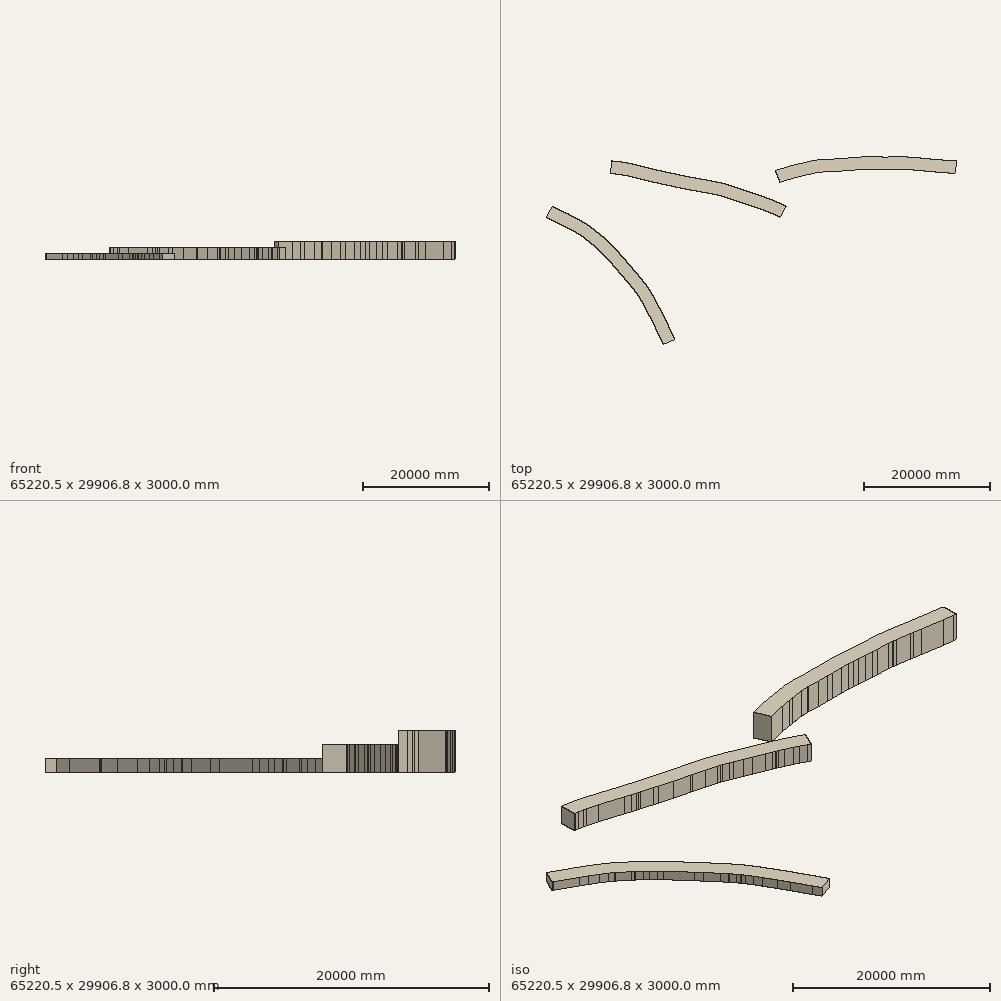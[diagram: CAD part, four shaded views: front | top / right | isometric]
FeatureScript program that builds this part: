
annotation { "Feature Type Name" : "Feature", "Feature Type Description" : "" }
export const myFeature = defineFeature(function(context is Context, id is Id, definition is map)
    precondition{}
    {
        {
            var Q0;
            Q0=qCreatedBy(makeId("Top.planeOp"),FACE);
            var sketch = newSketch(context, id + "F0", { "sketchPlane" : qUnion([Q0])});
            skLineSegment(sketch, "E0", {"start": v(-44615.33, 12253.54) * mm, "end": v(-44554.33, 12247.46) * mm});
            skLineSegment(sketch, "E1", {"start": v(-44554.33, 12247.46) * mm, "end": v(-44050.77, 12191.85) * mm});
            skLineSegment(sketch, "E2", {"start": v(-44050.77, 12191.85) * mm, "end": v(-43383.27, 12133.27) * mm});
            skLineSegment(sketch, "E3", {"start": v(-43383.27, 12133.27) * mm, "end": v(-43116.84, 12094.18) * mm});
            skLineSegment(sketch, "E4", {"start": v(-43116.84, 12094.18) * mm, "end": v(-41654.92, 11815.2) * mm});
            skLineSegment(sketch, "E5", {"start": v(-41654.92, 11815.2) * mm, "end": v(-38646.57, 11078.77) * mm});
            skLineSegment(sketch, "E6", {"start": v(-38646.57, 11078.77) * mm, "end": v(-37801.06, 10858.32) * mm});
            skLineSegment(sketch, "E7", {"start": v(-37801.06, 10858.32) * mm, "end": v(-37268.46, 10749.72) * mm});
            skLineSegment(sketch, "E8", {"start": v(-37268.46, 10749.72) * mm, "end": v(-37019.33, 10693.2) * mm});
            skLineSegment(sketch, "E9", {"start": v(-37019.33, 10693.2) * mm, "end": v(-36702.7, 10624.45) * mm});
            skLineSegment(sketch, "E10", {"start": v(-36702.7, 10624.45) * mm, "end": v(-35235, 10307.82) * mm});
            skLineSegment(sketch, "E11", {"start": v(-35235, 10307.82) * mm, "end": v(-34586.94, 10170.45) * mm});
            skLineSegment(sketch, "E12", {"start": v(-34586.94, 10170.45) * mm, "end": v(-32851.9, 9799.86) * mm});
            skLineSegment(sketch, "E13", {"start": v(-32851.9, 9799.86) * mm, "end": v(-30827.63, 9440.19) * mm});
            skLineSegment(sketch, "E14", {"start": v(-30827.63, 9440.19) * mm, "end": v(-30585.17, 9400.28) * mm});
            skLineSegment(sketch, "E15", {"start": v(-30585.17, 9400.28) * mm, "end": v(-28978.72, 9093.73) * mm});
            skLineSegment(sketch, "E16", {"start": v(-28978.72, 9093.73) * mm, "end": v(-27494.65, 8796.87) * mm});
            skLineSegment(sketch, "E17", {"start": v(-27494.65, 8796.87) * mm, "end": v(-27217.34, 8720.56) * mm});
            skLineSegment(sketch, "E18", {"start": v(-27217.34, 8720.56) * mm, "end": v(-26908.94, 8658.4) * mm});
            skLineSegment(sketch, "E19", {"start": v(-26908.94, 8658.4) * mm, "end": v(-26245.23, 8432.32) * mm});
            skLineSegment(sketch, "E20", {"start": v(-26245.23, 8432.32) * mm, "end": v(-25751.56, 8286.08) * mm});
            skLineSegment(sketch, "E21", {"start": v(-25751.56, 8286.08) * mm, "end": v(-24705.46, 7932.58) * mm});
            skLineSegment(sketch, "E22", {"start": v(-24705.46, 7932.58) * mm, "end": v(-23705.9, 7592.32) * mm});
            skLineSegment(sketch, "E23", {"start": v(-23705.9, 7592.32) * mm, "end": v(-22295.71, 7124.73) * mm});
            skLineSegment(sketch, "E24", {"start": v(-22295.71, 7124.73) * mm, "end": v(-21569.22, 6881.65) * mm});
            skLineSegment(sketch, "E25", {"start": v(-21569.22, 6881.65) * mm, "end": v(-21198.82, 6744) * mm});
            skLineSegment(sketch, "E26", {"start": v(-21198.82, 6744) * mm, "end": v(-21078.3, 6705.9) * mm});
            skLineSegment(sketch, "E27", {"start": v(-21078.3, 6705.9) * mm, "end": v(-20951.53, 6658.56) * mm});
            skLineSegment(sketch, "E28", {"start": v(-20951.53, 6658.56) * mm, "end": v(-20301.1, 6414.34) * mm});
            skLineSegment(sketch, "E29", {"start": v(-20301.1, 6414.34) * mm, "end": v(-19347.36, 6049.93) * mm});
            skLineSegment(sketch, "E30", {"start": v(-19347.36, 6049.93) * mm, "end": v(-18796.29, 5813.54) * mm});
            skLineSegment(sketch, "E31", {"start": v(-18796.29, 5813.54) * mm, "end": v(-18728.97, 5782.95) * mm});
            skLineSegment(sketch, "E32", {"start": v(-18728.97, 5782.95) * mm, "end": v(-17961.13, 5425.9) * mm});
            skLineSegment(sketch, "E33", {"start": v(-17961.13, 5425.9) * mm, "end": v(-17607.02, 5267.78) * mm});
            skLineSegment(sketch, "E34", {"start": v(-44472.78, 14249.25) * mm, "end": v(-44345.25, 14236.52) * mm});
            skLineSegment(sketch, "E35", {"start": v(-44345.25, 14236.52) * mm, "end": v(-43853.56, 14182.23) * mm});
            skLineSegment(sketch, "E36", {"start": v(-43853.56, 14182.23) * mm, "end": v(-43150.5, 14120.53) * mm});
            skLineSegment(sketch, "E37", {"start": v(-43150.5, 14120.53) * mm, "end": v(-42784.07, 14066.77) * mm});
            skLineSegment(sketch, "E38", {"start": v(-42784.07, 14066.77) * mm, "end": v(-41232.01, 13770.58) * mm});
            skLineSegment(sketch, "E39", {"start": v(-41232.01, 13770.58) * mm, "end": v(-41203.7, 13764.5) * mm});
            skLineSegment(sketch, "E40", {"start": v(-41203.7, 13764.5) * mm, "end": v(-41179.88, 13757.96) * mm});
            skLineSegment(sketch, "E41", {"start": v(-41179.88, 13757.96) * mm, "end": v(-38156.48, 13017.85) * mm});
            skLineSegment(sketch, "E42", {"start": v(-38156.48, 13017.85) * mm, "end": v(-37348.64, 12807.23) * mm});
            skLineSegment(sketch, "E43", {"start": v(-37348.64, 12807.23) * mm, "end": v(-36847.33, 12705) * mm});
            skLineSegment(sketch, "E44", {"start": v(-36847.33, 12705) * mm, "end": v(-36585.88, 12645.68) * mm});
            skLineSegment(sketch, "E45", {"start": v(-36585.88, 12645.68) * mm, "end": v(-36279.66, 12579.2) * mm});
            skLineSegment(sketch, "E46", {"start": v(-36279.66, 12579.2) * mm, "end": v(-34816.76, 12263.6) * mm});
            skLineSegment(sketch, "E47", {"start": v(-34816.76, 12263.6) * mm, "end": v(-34170.7, 12126.66) * mm});
            skLineSegment(sketch, "E48", {"start": v(-34170.7, 12126.66) * mm, "end": v(-32467.97, 11762.96) * mm});
            skLineSegment(sketch, "E49", {"start": v(-32467.97, 11762.96) * mm, "end": v(-30490.3, 11411.57) * mm});
            skLineSegment(sketch, "E50", {"start": v(-30490.3, 11411.57) * mm, "end": v(-30235.28, 11369.6) * mm});
            skLineSegment(sketch, "E51", {"start": v(-30235.28, 11369.6) * mm, "end": v(-28595.13, 11056.62) * mm});
            skLineSegment(sketch, "E52", {"start": v(-28595.13, 11056.62) * mm, "end": v(-27032.6, 10744.07) * mm});
            skLineSegment(sketch, "E53", {"start": v(-27032.6, 10744.07) * mm, "end": v(-26753.85, 10667.36) * mm});
            skLineSegment(sketch, "E54", {"start": v(-26753.85, 10667.36) * mm, "end": v(-26386.74, 10593.36) * mm});
            skLineSegment(sketch, "E55", {"start": v(-26386.74, 10593.36) * mm, "end": v(-25638.51, 10338.5) * mm});
            skLineSegment(sketch, "E56", {"start": v(-25638.51, 10338.5) * mm, "end": v(-25147.17, 10192.94) * mm});
            skLineSegment(sketch, "E57", {"start": v(-25147.17, 10192.94) * mm, "end": v(-24063.07, 9826.61) * mm});
            skLineSegment(sketch, "E58", {"start": v(-24063.07, 9826.61) * mm, "end": v(-23068.91, 9488.18) * mm});
            skLineSegment(sketch, "E59", {"start": v(-23068.91, 9488.18) * mm, "end": v(-21663.68, 9022.24) * mm});
            skLineSegment(sketch, "E60", {"start": v(-21663.68, 9022.24) * mm, "end": v(-20903.37, 8767.85) * mm});
            skLineSegment(sketch, "E61", {"start": v(-20903.37, 8767.85) * mm, "end": v(-20548.7, 8636.04) * mm});
            skLineSegment(sketch, "E62", {"start": v(-20548.7, 8636.04) * mm, "end": v(-20426.65, 8597.46) * mm});
            skLineSegment(sketch, "E63", {"start": v(-20426.65, 8597.46) * mm, "end": v(-20250.15, 8531.54) * mm});
            skLineSegment(sketch, "E64", {"start": v(-20250.15, 8531.54) * mm, "end": v(-19592.66, 8284.67) * mm});
            skLineSegment(sketch, "E65", {"start": v(-19592.66, 8284.67) * mm, "end": v(-18595.92, 7903.83) * mm});
            skLineSegment(sketch, "E66", {"start": v(-18595.92, 7903.83) * mm, "end": v(-17988.24, 7643.16) * mm});
            skLineSegment(sketch, "E67", {"start": v(-17988.24, 7643.16) * mm, "end": v(-17893.58, 7600.15) * mm});
            skLineSegment(sketch, "E68", {"start": v(-17893.58, 7600.15) * mm, "end": v(-17131.71, 7245.87) * mm});
            skLineSegment(sketch, "E69", {"start": v(-17131.71, 7245.87) * mm, "end": v(-16748.38, 7074.7) * mm});
            skLineSegment(sketch, "E70", {"start": v(-16748.38, 7074.7) * mm, "end": v(-16718.32, 7062.38) * mm});
            skLineSegment(sketch, "E71", {"start": v(-16718.32, 7062.38) * mm, "end": v(-16653.46, 7029.8) * mm});
            skLineSegment(sketch, "E72", {"start": v(-34368.58, -14174.47) * mm, "end": v(-36213.48, -14953.42) * mm});
            skLineSegment(sketch, "E73", {"start": v(-54819.93, 5267.79) * mm, "end": v(-54768.7, 5244.91) * mm});
            skLineSegment(sketch, "E74", {"start": v(-54768.7, 5244.91) * mm, "end": v(-54672, 5196.33) * mm});
            skLineSegment(sketch, "E75", {"start": v(-54672, 5196.33) * mm, "end": v(-52152.07, 3947.35) * mm});
            skLineSegment(sketch, "E76", {"start": v(-52152.07, 3947.35) * mm, "end": v(-51311.75, 3513.66) * mm});
            skLineSegment(sketch, "E77", {"start": v(-51311.75, 3513.66) * mm, "end": v(-50310.39, 2976.03) * mm});
            skLineSegment(sketch, "E78", {"start": v(-50310.39, 2976.03) * mm, "end": v(-49491.42, 2480.31) * mm});
            skLineSegment(sketch, "E79", {"start": v(-49491.42, 2480.31) * mm, "end": v(-48990.85, 2146.87) * mm});
            skLineSegment(sketch, "E80", {"start": v(-48990.85, 2146.87) * mm, "end": v(-48868.16, 2044.67) * mm});
            skLineSegment(sketch, "E81", {"start": v(-48868.16, 2044.67) * mm, "end": v(-47592.88, 1022.1) * mm});
            skLineSegment(sketch, "E82", {"start": v(-47592.88, 1022.1) * mm, "end": v(-47412.3, 882.4) * mm});
            skLineSegment(sketch, "E83", {"start": v(-47412.3, 882.4) * mm, "end": v(-47307.21, 794.3) * mm});
            skLineSegment(sketch, "E84", {"start": v(-47307.21, 794.3) * mm, "end": v(-46679.03, 253.82) * mm});
            skLineSegment(sketch, "E85", {"start": v(-46679.03, 253.82) * mm, "end": v(-46250.8, -159.2) * mm});
            skLineSegment(sketch, "E86", {"start": v(-46250.8, -159.2) * mm, "end": v(-45637.7, -753.6) * mm});
            skLineSegment(sketch, "E87", {"start": v(-45637.7, -753.6) * mm, "end": v(-45238.63, -1180.77) * mm});
            skLineSegment(sketch, "E88", {"start": v(-45238.63, -1180.77) * mm, "end": v(-43190.08, -3537.34) * mm});
            skLineSegment(sketch, "E89", {"start": v(-43190.08, -3537.34) * mm, "end": v(-42577.39, -4247.8) * mm});
            skLineSegment(sketch, "E90", {"start": v(-42577.39, -4247.8) * mm, "end": v(-41450, -5579.83) * mm});
            skLineSegment(sketch, "E91", {"start": v(-41450, -5579.83) * mm, "end": v(-40980.1, -6165.94) * mm});
            skLineSegment(sketch, "E92", {"start": v(-40980.1, -6165.94) * mm, "end": v(-40899.18, -6270.95) * mm});
            skLineSegment(sketch, "E93", {"start": v(-40899.18, -6270.95) * mm, "end": v(-40488.2, -6827.58) * mm});
            skLineSegment(sketch, "E94", {"start": v(-40488.2, -6827.58) * mm, "end": v(-40211.82, -7203.77) * mm});
            skLineSegment(sketch, "E95", {"start": v(-40211.82, -7203.77) * mm, "end": v(-40139.03, -7324.5) * mm});
            skLineSegment(sketch, "E96", {"start": v(-40139.03, -7324.5) * mm, "end": v(-39948.96, -7649.3) * mm});
            skLineSegment(sketch, "E97", {"start": v(-39948.96, -7649.3) * mm, "end": v(-39526.47, -8326.14) * mm});
            skLineSegment(sketch, "E98", {"start": v(-39526.47, -8326.14) * mm, "end": v(-39088.12, -9185.47) * mm});
            skLineSegment(sketch, "E99", {"start": v(-39088.12, -9185.47) * mm, "end": v(-38311.38, -10642.52) * mm});
            skLineSegment(sketch, "E100", {"start": v(-38311.38, -10642.52) * mm, "end": v(-37716.13, -11836.56) * mm});
            skLineSegment(sketch, "E101", {"start": v(-37716.13, -11836.56) * mm, "end": v(-37688.19, -11897.84) * mm});
            skLineSegment(sketch, "E102", {"start": v(-37688.19, -11897.84) * mm, "end": v(-36656.55, -14037.35) * mm});
            skLineSegment(sketch, "E103", {"start": v(-36656.55, -14037.35) * mm, "end": v(-36213.48, -14953.42) * mm});
            skLineSegment(sketch, "E104", {"start": v(-53866.37, 7029.8) * mm, "end": v(-53779.01, 6985.92) * mm});
            skLineSegment(sketch, "E105", {"start": v(-53779.01, 6985.92) * mm, "end": v(-51249.3, 5732.08) * mm});
            skLineSegment(sketch, "E106", {"start": v(-51249.3, 5732.08) * mm, "end": v(-50380.03, 5283.45) * mm});
            skLineSegment(sketch, "E107", {"start": v(-50380.03, 5283.45) * mm, "end": v(-49318.87, 4713.72) * mm});
            skLineSegment(sketch, "E108", {"start": v(-49318.87, 4713.72) * mm, "end": v(-48418.7, 4168.85) * mm});
            skLineSegment(sketch, "E109", {"start": v(-48418.7, 4168.85) * mm, "end": v(-47793, 3752.05) * mm});
            skLineSegment(sketch, "E110", {"start": v(-47793, 3752.05) * mm, "end": v(-47602.44, 3593.31) * mm});
            skLineSegment(sketch, "E111", {"start": v(-47602.44, 3593.31) * mm, "end": v(-46355.3, 2593.31) * mm});
            skLineSegment(sketch, "E112", {"start": v(-46355.3, 2593.31) * mm, "end": v(-46157.51, 2440.29) * mm});
            skLineSegment(sketch, "E113", {"start": v(-46157.51, 2440.29) * mm, "end": v(-46012.55, 2318.78) * mm});
            skLineSegment(sketch, "E114", {"start": v(-46012.55, 2318.78) * mm, "end": v(-45331.52, 1732.82) * mm});
            skLineSegment(sketch, "E115", {"start": v(-45331.52, 1732.82) * mm, "end": v(-44860.53, 1278.54) * mm});
            skLineSegment(sketch, "E116", {"start": v(-44860.53, 1278.54) * mm, "end": v(-44210.02, 647.9) * mm});
            skLineSegment(sketch, "E117", {"start": v(-44210.02, 647.9) * mm, "end": v(-43752.7, 158.38) * mm});
            skLineSegment(sketch, "E118", {"start": v(-43752.7, 158.38) * mm, "end": v(-41678.07, -2228.2) * mm});
            skLineSegment(sketch, "E119", {"start": v(-41678.07, -2228.2) * mm, "end": v(-41056.76, -2948.65) * mm});
            skLineSegment(sketch, "E120", {"start": v(-41056.76, -2948.65) * mm, "end": v(-39906.2, -4308.05) * mm});
            skLineSegment(sketch, "E121", {"start": v(-39906.2, -4308.05) * mm, "end": v(-39407.61, -4929.95) * mm});
            skLineSegment(sketch, "E122", {"start": v(-39407.61, -4929.95) * mm, "end": v(-39302.4, -5066.49) * mm});
            skLineSegment(sketch, "E123", {"start": v(-39302.4, -5066.49) * mm, "end": v(-38877.84, -5641.52) * mm});
            skLineSegment(sketch, "E124", {"start": v(-38877.84, -5641.52) * mm, "end": v(-38546.08, -6093.09) * mm});
            skLineSegment(sketch, "E125", {"start": v(-38546.08, -6093.09) * mm, "end": v(-38419.48, -6303.08) * mm});
            skLineSegment(sketch, "E126", {"start": v(-38419.48, -6303.08) * mm, "end": v(-38237.24, -6614.49) * mm});
            skLineSegment(sketch, "E127", {"start": v(-38237.24, -6614.49) * mm, "end": v(-37784.13, -7340.39) * mm});
            skLineSegment(sketch, "E128", {"start": v(-37784.13, -7340.39) * mm, "end": v(-37314.74, -8260.57) * mm});
            skLineSegment(sketch, "E129", {"start": v(-37314.74, -8260.57) * mm, "end": v(-36533.65, -9725.78) * mm});
            skLineSegment(sketch, "E130", {"start": v(-36533.65, -9725.78) * mm, "end": v(-35948.1, -10900.34) * mm});
            skLineSegment(sketch, "E131", {"start": v(-35948.1, -10900.34) * mm, "end": v(-35930.52, -10930.07) * mm});
            skLineSegment(sketch, "E132", {"start": v(-35930.52, -10930.07) * mm, "end": v(-35908.26, -10980.72) * mm});
            skLineSegment(sketch, "E133", {"start": v(-35908.26, -10980.72) * mm, "end": v(-35877.3, -11048.62) * mm});
            skLineSegment(sketch, "E134", {"start": v(-35877.3, -11048.62) * mm, "end": v(-34855.56, -13167.61) * mm});
            skLineSegment(sketch, "E135", {"start": v(-34855.56, -13167.61) * mm, "end": v(-34368.58, -14174.47) * mm});
            skLineSegment(sketch, "E136", {"start": v(-17687.08, 10827.1) * mm, "end": v(-15581.3, 11478.69) * mm});
            skLineSegment(sketch, "E137", {"start": v(-15581.3, 11478.69) * mm, "end": v(-14218.4, 11821.37) * mm});
            skLineSegment(sketch, "E138", {"start": v(-14218.4, 11821.37) * mm, "end": v(-13546.71, 11973.07) * mm});
            skLineSegment(sketch, "E139", {"start": v(-13546.71, 11973.07) * mm, "end": v(-11990.59, 12338.15) * mm});
            skLineSegment(sketch, "E140", {"start": v(-11990.59, 12338.15) * mm, "end": v(-10949.85, 12476.65) * mm});
            skLineSegment(sketch, "E141", {"start": v(-10949.85, 12476.65) * mm, "end": v(-10860.75, 12484.02) * mm});
            skLineSegment(sketch, "E142", {"start": v(-10860.75, 12484.02) * mm, "end": v(-10778.37, 12489.67) * mm});
            skLineSegment(sketch, "E143", {"start": v(-10778.37, 12489.67) * mm, "end": v(-9255.98, 12528.04) * mm});
            skLineSegment(sketch, "E144", {"start": v(-9255.98, 12528.04) * mm, "end": v(-7842.16, 12642.42) * mm});
            skLineSegment(sketch, "E145", {"start": v(-7842.16, 12642.42) * mm, "end": v(-7071.04, 12676.84) * mm});
            skLineSegment(sketch, "E146", {"start": v(-7071.04, 12676.84) * mm, "end": v(-5740.54, 12798.87) * mm});
            skLineSegment(sketch, "E147", {"start": v(-5740.54, 12798.87) * mm, "end": v(-4709.51, 12870.5) * mm});
            skLineSegment(sketch, "E148", {"start": v(-4709.51, 12870.5) * mm, "end": v(-3963.6, 12890.43) * mm});
            skLineSegment(sketch, "E149", {"start": v(-3963.6, 12890.43) * mm, "end": v(-3230.1, 12893.67) * mm});
            skLineSegment(sketch, "E150", {"start": v(-3230.1, 12893.67) * mm, "end": v(-2138.56, 12890.7) * mm});
            skLineSegment(sketch, "E151", {"start": v(-2138.56, 12890.7) * mm, "end": v(-1135.73, 12866.6) * mm});
            skLineSegment(sketch, "E152", {"start": v(-1135.73, 12866.6) * mm, "end": v(-447.19, 12871.13) * mm});
            skLineSegment(sketch, "E153", {"start": v(-447.19, 12871.13) * mm, "end": v(1157.72, 12950.91) * mm});
            skLineSegment(sketch, "E154", {"start": v(1157.72, 12950.91) * mm, "end": v(1782.92, 12919.34) * mm});
            skLineSegment(sketch, "E155", {"start": v(1782.92, 12919.34) * mm, "end": v(1895.39, 12915.36) * mm});
            skLineSegment(sketch, "E156", {"start": v(1895.39, 12915.36) * mm, "end": v(2213.54, 12893.35) * mm});
            skLineSegment(sketch, "E157", {"start": v(2213.54, 12893.35) * mm, "end": v(4110.01, 12768.9) * mm});
            skLineSegment(sketch, "E158", {"start": v(4110.01, 12768.9) * mm, "end": v(4481.75, 12721.43) * mm});
            skLineSegment(sketch, "E159", {"start": v(4481.75, 12721.43) * mm, "end": v(5599.82, 12611.7) * mm});
            skLineSegment(sketch, "E160", {"start": v(5599.82, 12611.7) * mm, "end": v(8480.2, 12360.07) * mm});
            skLineSegment(sketch, "E161", {"start": v(8480.2, 12360.07) * mm, "end": v(9829.67, 12296.3) * mm});
            skLineSegment(sketch, "E162", {"start": v(9829.67, 12296.3) * mm, "end": v(10258.04, 12253.55) * mm});
            skLineSegment(sketch, "E163", {"start": v(-18399.03, 12696.1) * mm, "end": v(-18238.8, 12764.65) * mm});
            skLineSegment(sketch, "E164", {"start": v(-18238.8, 12764.65) * mm, "end": v(-18169.82, 12771.3) * mm});
            skLineSegment(sketch, "E165", {"start": v(-18169.82, 12771.3) * mm, "end": v(-16121.12, 13405.2) * mm});
            skLineSegment(sketch, "E166", {"start": v(-16121.12, 13405.2) * mm, "end": v(-14682.61, 13766.9) * mm});
            skLineSegment(sketch, "E167", {"start": v(-14682.61, 13766.9) * mm, "end": v(-13995.43, 13922.1) * mm});
            skLineSegment(sketch, "E168", {"start": v(-13995.43, 13922.1) * mm, "end": v(-12351.78, 14307.72) * mm});
            skLineSegment(sketch, "E169", {"start": v(-12351.78, 14307.72) * mm, "end": v(-11164.4, 14465.73) * mm});
            skLineSegment(sketch, "E170", {"start": v(-11164.4, 14465.73) * mm, "end": v(-11011.64, 14478.37) * mm});
            skLineSegment(sketch, "E171", {"start": v(-11011.64, 14478.37) * mm, "end": v(-10871.98, 14487.94) * mm});
            skLineSegment(sketch, "E172", {"start": v(-10871.98, 14487.94) * mm, "end": v(-9361.9, 14526) * mm});
            skLineSegment(sketch, "E173", {"start": v(-9361.9, 14526) * mm, "end": v(-7967.42, 14638.82) * mm});
            skLineSegment(sketch, "E174", {"start": v(-7967.42, 14638.82) * mm, "end": v(-7207.04, 14672.76) * mm});
            skLineSegment(sketch, "E175", {"start": v(-7207.04, 14672.76) * mm, "end": v(-5901.21, 14792.53) * mm});
            skLineSegment(sketch, "E176", {"start": v(-5901.21, 14792.53) * mm, "end": v(-4805.57, 14868.66) * mm});
            skLineSegment(sketch, "E177", {"start": v(-4805.57, 14868.66) * mm, "end": v(-3994.7, 14890.31) * mm});
            skLineSegment(sketch, "E178", {"start": v(-3994.7, 14890.31) * mm, "end": v(-3231.79, 14893.68) * mm});
            skLineSegment(sketch, "E179", {"start": v(-3231.79, 14893.68) * mm, "end": v(-2111.8, 14890.63) * mm});
            skLineSegment(sketch, "E180", {"start": v(-2111.8, 14890.63) * mm, "end": v(-1118.3, 14866.75) * mm});
            skLineSegment(sketch, "E181", {"start": v(-1118.3, 14866.75) * mm, "end": v(-503.45, 14870.8) * mm});
            skLineSegment(sketch, "E182", {"start": v(-503.45, 14870.8) * mm, "end": v(1158.5, 14953.42) * mm});
            skLineSegment(sketch, "E183", {"start": v(1158.5, 14953.42) * mm, "end": v(1868.72, 14917.56) * mm});
            skLineSegment(sketch, "E184", {"start": v(1868.72, 14917.56) * mm, "end": v(1999.81, 14912.92) * mm});
            skLineSegment(sketch, "E185", {"start": v(1999.81, 14912.92) * mm, "end": v(2348.06, 14888.82) * mm});
            skLineSegment(sketch, "E186", {"start": v(2348.06, 14888.82) * mm, "end": v(4302.34, 14760.58) * mm});
            skLineSegment(sketch, "E187", {"start": v(4302.34, 14760.58) * mm, "end": v(4706.14, 14709.01) * mm});
            skLineSegment(sketch, "E188", {"start": v(4706.14, 14709.01) * mm, "end": v(5784.52, 14603.18) * mm});
            skLineSegment(sketch, "E189", {"start": v(5784.52, 14603.18) * mm, "end": v(8614.49, 14355.96) * mm});
            skLineSegment(sketch, "E190", {"start": v(8614.49, 14355.96) * mm, "end": v(9976.29, 14291.6) * mm});
            skLineSegment(sketch, "E191", {"start": v(9976.29, 14291.6) * mm, "end": v(10400.6, 14249.26) * mm});
            skLineSegment(sketch, "E192", {"start": v(-54819.93, 5267.79) * mm, "end": v(-53866.37, 7029.8) * mm});
            skLineSegment(sketch, "E193", {"start": v(-44615.33, 12253.54) * mm, "end": v(-44472.78, 14249.25) * mm});
            skLineSegment(sketch, "E194", {"start": v(-17607.02, 5267.78) * mm, "end": v(-16653.46, 7029.8) * mm});
            skLineSegment(sketch, "E195", {"start": v(-18399.03, 12696.1) * mm, "end": v(-17687.08, 10827.1) * mm});
            skLineSegment(sketch, "E196", {"start": v(10258.04, 12253.55) * mm, "end": v(10400.6, 14249.26) * mm});
            skSolve(sketch);
        }
        {
            var Q0;
            Q0=makeQuery(id+"F0.imprint","IMPRINT",FACE,{"disambiguationData":[TD([[makeQuery(id+"F0.imprint","IMPRINT",EDGE,{"derivedFrom":sQuery(id+"F0.wireOp",EDGE,"E72")}),-1.0]])]});
            extrude(context, id + "F1", {"entities" : qUnion([Q0]), "depth" : 1000 * mm, "offsetDistance" : 25 * mm});
        }
        {
            var Q0;
            Q0=makeQuery(id+"F0.imprint","IMPRINT",FACE,{"disambiguationData":[TD([[makeQuery(id+"F0.imprint","IMPRINT",EDGE,{"derivedFrom":sQuery(id+"F0.wireOp",EDGE,"E0")}),1.0]])]});
            extrude(context, id + "F2", {"entities" : qUnion([Q0]), "depth" : 2000 * mm, "offsetDistance" : 25 * mm});
        }
        {
            var Q0;
            Q0=makeQuery(id+"F0.imprint","IMPRINT",FACE,{"disambiguationData":[TD([[makeQuery(id+"F0.imprint","IMPRINT",EDGE,{"derivedFrom":sQuery(id+"F0.wireOp",EDGE,"E136")}),1.0]])]});
            extrude(context, id + "F3", {"entities" : qUnion([Q0]), "depth" : 3000 * mm, "offsetDistance" : 25 * mm});
        }
    });
